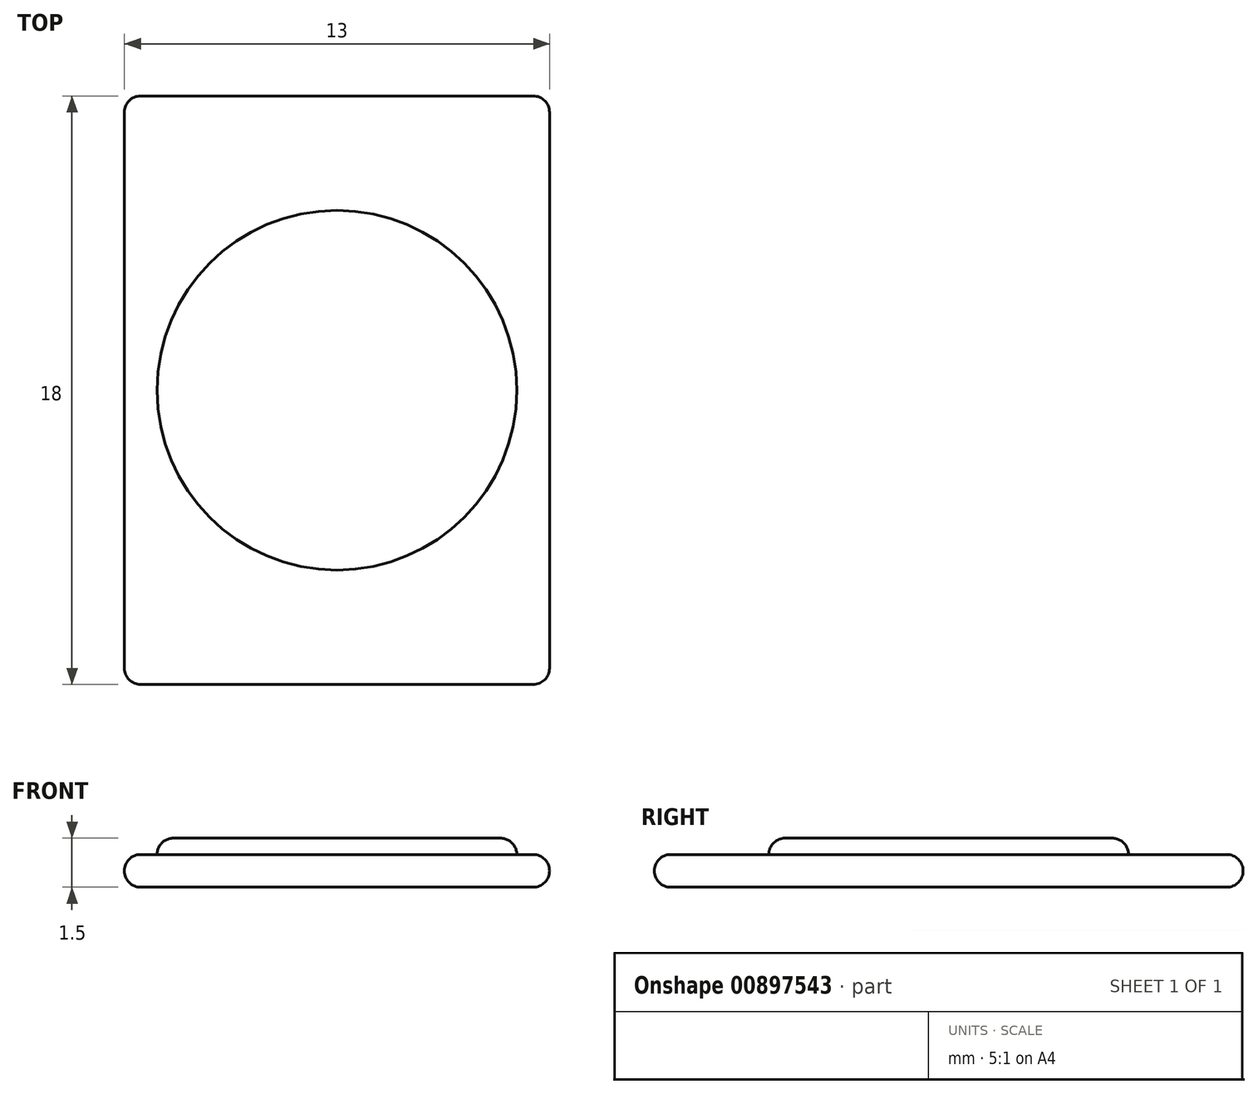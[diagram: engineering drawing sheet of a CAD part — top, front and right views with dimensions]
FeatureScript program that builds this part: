
annotation { "Feature Type Name" : "Feature", "Feature Type Description" : "" }
export const myFeature = defineFeature(function(context is Context, id is Id, definition is map)
    precondition{}
    {
        {
            var Q0;
            Q0=qCreatedBy(makeId("Top.planeOp"),FACE);
            var sketch = newSketch(context, id + "F0", { "sketchPlane" : qUnion([Q0])});
            skLineSegment(sketch, "E0.bottom", {"start": v(-35.38, 42.07) * mm, "end": v(-22.38, 42.07) * mm});
            skLineSegment(sketch, "E0.top", {"start": v(-35.38, 24.07) * mm, "end": v(-22.38, 24.07) * mm});
            skLineSegment(sketch, "E0.left", {"start": v(-35.38, 42.07) * mm, "end": v(-35.38, 24.07) * mm});
            skLineSegment(sketch, "E0.right", {"start": v(-22.38, 42.07) * mm, "end": v(-22.38, 24.07) * mm});
            skSolve(sketch);
        }
        {
            var Q0;
            Q0=makeQuery(id+"F0.imprint","IMPRINT",FACE,{"disambiguationData":[TD([[makeQuery(id+"F0.imprint","IMPRINT",EDGE,{"derivedFrom":sQuery(id+"F0.wireOp",EDGE,"E0.bottom")}),-1.0]])]});
            extrude(context, id + "F1", {"entities" : qUnion([Q0]), "depth" : 1 * mm, "offsetDistance" : 25 * mm});
        }
        {
            var Q0;
            Q0=makeQuery(id+"F1.opExtrude","CAP_FACE",FACE,{"disambiguationData":[OSD([sQuery(id+"F0.wireOp",EDGE,"E0.bottom"),sQuery(id+"F0.wireOp",EDGE,"E0.top"),sQuery(id+"F0.wireOp",EDGE,"E0.left"),sQuery(id+"F0.wireOp",EDGE,"E0.right")])],"isStart":false});
            var sketch = newSketch(context, id + "F2", { "sketchPlane" : qUnion([Q0])});
            skCircle(sketch, "E1", {"center": v(-28.88, 33.07) * mm, "radius": 5.5 * mm});
            skPoint(sketch, "E1.centerSnap0", {"position": v(-22.38, 33.07) * mm});
            skPoint(sketch, "E1.centerSnap1", {"position": v(-28.88, 42.07) * mm});
            skSolve(sketch);
        }
        {
            var Q0;
            Q0 = qSketchRegion(id + "F2", true);
            extrude(context, id + "F3", {"entities" : qUnion([Q0]), "operationType" : NewBodyOperationType.ADD, "depth" : 0.5 * mm, "offsetDistance" : 25 * mm});
        }
        {
            var Q0;
            Q0=makeQuery(id+"F1.opExtrude","CAP_EDGE",EDGE,{"disambiguationData":[OSD([sQuery(id+"F0.wireOp",EDGE,"E0.bottom")])],"isStart":false});
            var Q1;
            Q1=makeQuery(id+"F1.opExtrude","CAP_EDGE",EDGE,{"disambiguationData":[OSD([sQuery(id+"F0.wireOp",EDGE,"E0.bottom")])],"isStart":true});
            var Q2;
            Q2=makeQuery(id+"F1.opExtrude","CAP_EDGE",EDGE,{"disambiguationData":[OSD([sQuery(id+"F0.wireOp",EDGE,"E0.left")])],"isStart":false});
            var Q3;
            Q3=makeQuery(id+"F1.opExtrude","CAP_EDGE",EDGE,{"disambiguationData":[OSD([sQuery(id+"F0.wireOp",EDGE,"E0.right")])],"isStart":false});
            var Q4;
            Q4=makeQuery(id+"F1.opExtrude","CAP_EDGE",EDGE,{"disambiguationData":[OSD([sQuery(id+"F0.wireOp",EDGE,"E0.top")])],"isStart":false});
            var Q5;
            Q5=makeQuery(id+"F3.opExtrude","CAP_EDGE",EDGE,{"disambiguationData":[OSD([sQuery(id+"F2.wireOp",EDGE,"E1")])],"isStart":false});
            var Q6;
            Q6=makeQuery(id+"F1.opExtrude","SWEPT_EDGE",EDGE,{"disambiguationData":[OSD([sQuery(id+"F0.wireOp",EDGE,"E0.bottom"),sQuery(id+"F0.wireOp",EDGE,"E0.right")])]});
            var Q7;
            Q7=makeQuery(id+"F1.opExtrude","CAP_EDGE",EDGE,{"disambiguationData":[OSD([sQuery(id+"F0.wireOp",EDGE,"E0.right")])],"isStart":true});
            var Q8;
            Q8=makeQuery(id+"F1.opExtrude","CAP_EDGE",EDGE,{"disambiguationData":[OSD([sQuery(id+"F0.wireOp",EDGE,"E0.left")])],"isStart":true});
            var Q9;
            Q9=makeQuery(id+"F1.opExtrude","CAP_EDGE",EDGE,{"disambiguationData":[OSD([sQuery(id+"F0.wireOp",EDGE,"E0.top")])],"isStart":true});
            var Q10;
            Q10=makeQuery(id+"F1.opExtrude","SWEPT_EDGE",EDGE,{"disambiguationData":[OSD([sQuery(id+"F0.wireOp",EDGE,"E0.top"),sQuery(id+"F0.wireOp",EDGE,"E0.right")])]});
            var Q11;
            Q11=makeQuery(id+"F1.opExtrude","SWEPT_EDGE",EDGE,{"disambiguationData":[OSD([sQuery(id+"F0.wireOp",EDGE,"E0.top"),sQuery(id+"F0.wireOp",EDGE,"E0.left")])]});
            var Q12;
            Q12=makeQuery(id+"F1.opExtrude","SWEPT_EDGE",EDGE,{"disambiguationData":[OSD([sQuery(id+"F0.wireOp",EDGE,"E0.bottom"),sQuery(id+"F0.wireOp",EDGE,"E0.left")])]});
            fillet(context, id + "F4", {"entities" : qUnion([Q0, Q1, Q2, Q3, Q4, Q5, Q6, Q7, Q8, Q9, Q10, Q11, Q12]), "radius" : 0.5 * mm, "tangentPropagation" : true, "allowEdgeOverflow" : false});
        }
    });
